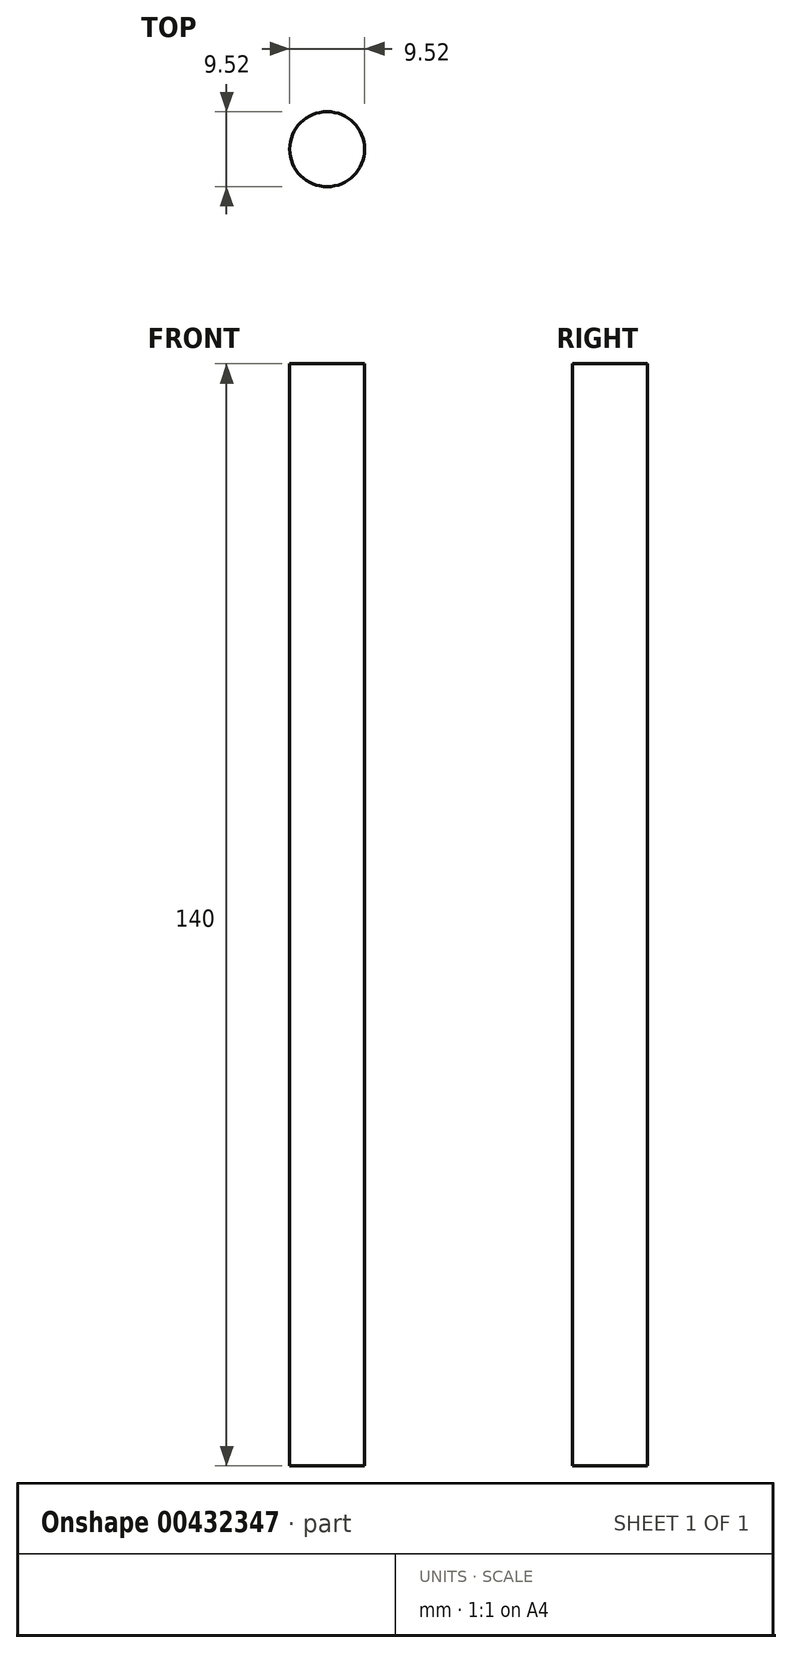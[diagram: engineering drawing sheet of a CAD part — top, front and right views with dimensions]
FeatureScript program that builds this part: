
annotation { "Feature Type Name" : "Feature", "Feature Type Description" : "" }
export const myFeature = defineFeature(function(context is Context, id is Id, definition is map)
    precondition{}
    {
        {
            var Q0;
            Q0=qCreatedBy(makeId("Top.planeOp"),FACE);
            var sketch = newSketch(context, id + "F0", { "sketchPlane" : qUnion([Q0])});
            skCircle(sketch, "E0", {"center": v(0, 0) * mm, "radius": 4.76 * mm});
            skSolve(sketch);
        }
        {
            var Q0;
            Q0 = qSketchRegion(id + "F0", true);
            extrude(context, id + "F1", {"entities" : qUnion([Q0]), "depth" : 140 * mm});
        }
    });
